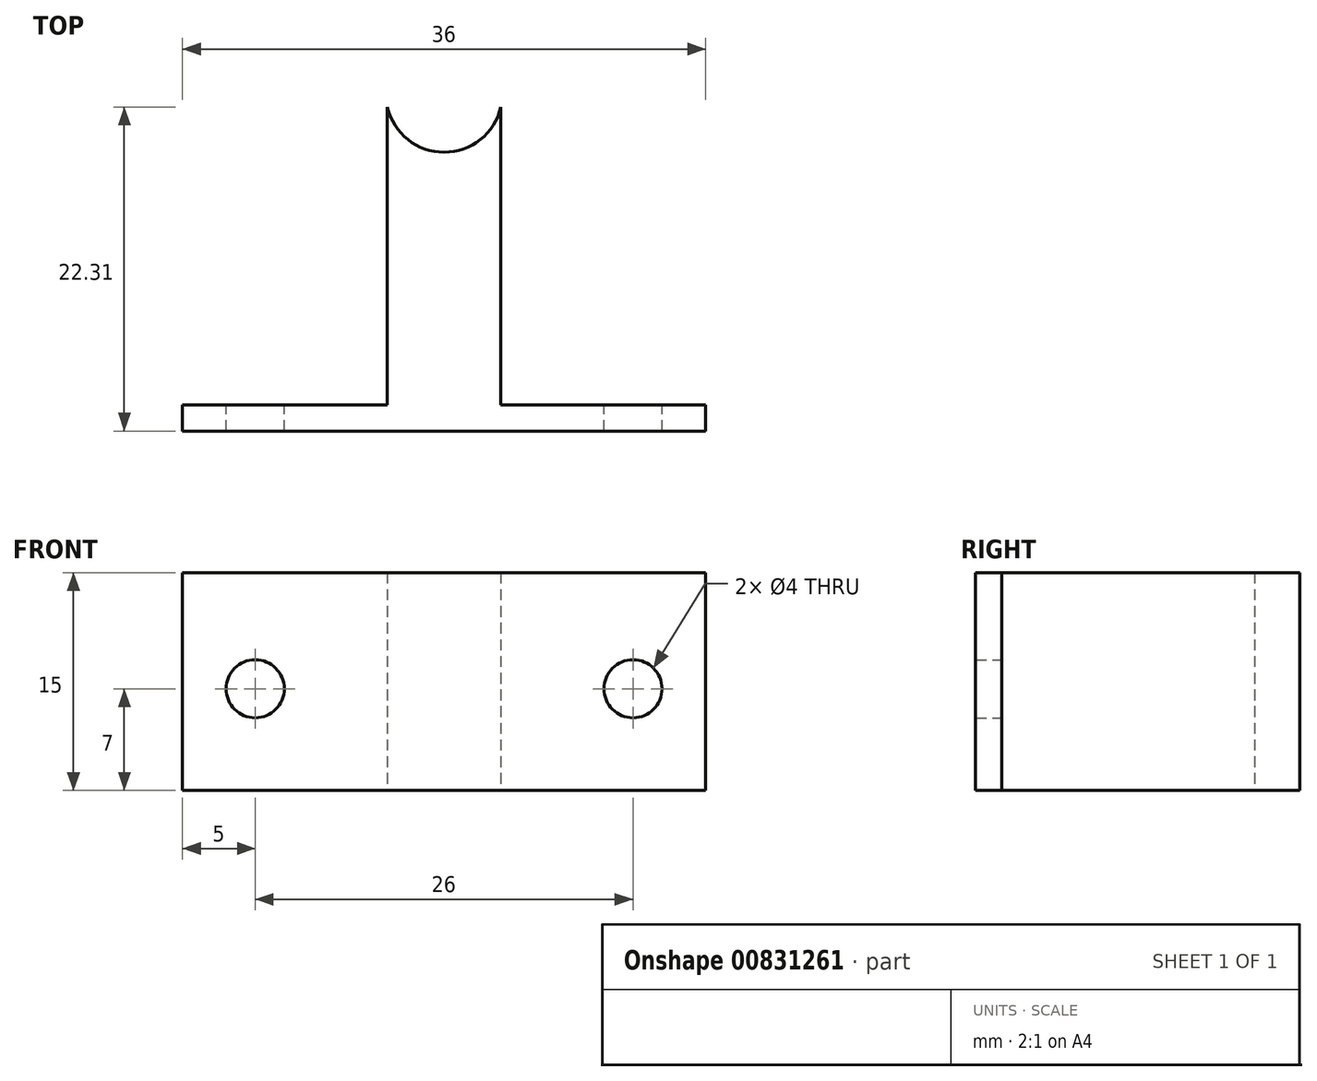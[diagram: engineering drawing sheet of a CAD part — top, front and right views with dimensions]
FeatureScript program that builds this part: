
annotation { "Feature Type Name" : "Feature", "Feature Type Description" : "" }
export const myFeature = defineFeature(function(context is Context, id is Id, definition is map)
    precondition{}
    {
        {
            var Q0;
            Q0=qCreatedBy(makeId("Top.planeOp"),FACE);
            var sketch = newSketch(context, id + "F0", { "sketchPlane" : qUnion([Q0])});
            skLineSegment(sketch, "E0.bottom", {"start": v(-18, -0.9) * mm, "end": v(18, -0.9) * mm});
            skLineSegment(sketch, "E0.top", {"start": v(-18, 0.9) * mm, "end": v(-3.9, 0.9) * mm});
            skLineSegment(sketch, "E0.left", {"start": v(-18, -0.9) * mm, "end": v(-18, 0.9) * mm});
            skLineSegment(sketch, "E0.right", {"start": v(18, -0.9) * mm, "end": v(18, 0.9) * mm});
            skPoint(sketch, "E0.middle", {"position": v(0, 0) * mm});
            skLineSegment(sketch, "E1", {"start": v(-3.9, 0.9) * mm, "end": v(-3.9, 21.41) * mm, "construction": true});
            skLineSegment(sketch, "E2", {"start": v(-3.9, 22.3) * mm, "end": v(3.9, 22.3) * mm, "construction": true});
            skLineSegment(sketch, "E3", {"start": v(3.9, 21.41) * mm, "end": v(3.9, 0.9) * mm, "construction": true});
            skLineSegment(sketch, "E4", {"start": v(-3.9, 21.41) * mm, "end": v(-3.9, 0.9) * mm});
            skLineSegment(sketch, "E5", {"start": v(3.9, 21.41) * mm, "end": v(3.9, 0.9) * mm});
            skArc(sketch, "E6", {"start": v(-3.9, 21.41) * mm, "mid": v(0, 18.3) * mm, "end": v(3.9, 21.41) * mm});
            skLineSegment(sketch, "E7.trimOffspring", {"start": v(3.9, 0.9) * mm, "end": v(18, 0.9) * mm});
            skSolve(sketch);
        }
        {
            var Q0;
            Q0=makeQuery(id+"F0.imprint","IMPRINT",FACE,{"disambiguationData":[TD([[makeQuery(id+"F0.imprint","IMPRINT",EDGE,{"derivedFrom":sQuery(id+"F0.wireOp",EDGE,"E0.bottom")}),1.0]])]});
            extrude(context, id + "F1", {"entities" : qUnion([Q0]), "depth" : 15 * mm, "offsetDistance" : 25 * mm});
        }
        {
            var Q0;
            Q0=makeQuery(id+"F1.opExtrude","SWEPT_FACE",FACE,{"disambiguationData":[OSD([sQuery(id+"F0.wireOp",EDGE,"E7.trimOffspring")])]});
            var sketch = newSketch(context, id + "F2", { "sketchPlane" : qUnion([Q0])});
            skLineSegment(sketch, "E8", {"start": v(-20.58, 7) * mm, "end": v(21, 7) * mm, "construction": true});
            skLineSegment(sketch, "E9", {"start": v(-13, 15.06) * mm, "end": v(-13, -0.7) * mm, "construction": true});
            skLineSegment(sketch, "E10", {"start": v(13, 15.61) * mm, "end": v(13, -0.7) * mm, "construction": true});
            skCircle(sketch, "E11", {"center": v(-13, 7) * mm, "radius": 2 * mm});
            skCircle(sketch, "E12", {"center": v(13, 7) * mm, "radius": 2 * mm});
            skSolve(sketch);
        }
        {
            var Q0;
            Q0=makeQuery(id+"F2.imprint","IMPRINT",FACE,{"disambiguationData":[TD([[makeQuery(id+"F2.imprint","IMPRINT",EDGE,{"derivedFrom":sQuery(id+"F2.wireOp",EDGE,"E11")}),1.0]])]});
            var Q1;
            Q1=makeQuery(id+"F2.imprint","IMPRINT",FACE,{"disambiguationData":[TD([[makeQuery(id+"F2.imprint","IMPRINT",EDGE,{"derivedFrom":sQuery(id+"F2.wireOp",EDGE,"E12")}),1.0]])]});
            extrude(context, id + "F3", {"entities" : qUnion([Q0, Q1]), "operationType" : NewBodyOperationType.REMOVE, "oppositeDirection" : true, "depth" : 3 * mm, "offsetDistance" : 25 * mm});
        }
    });
